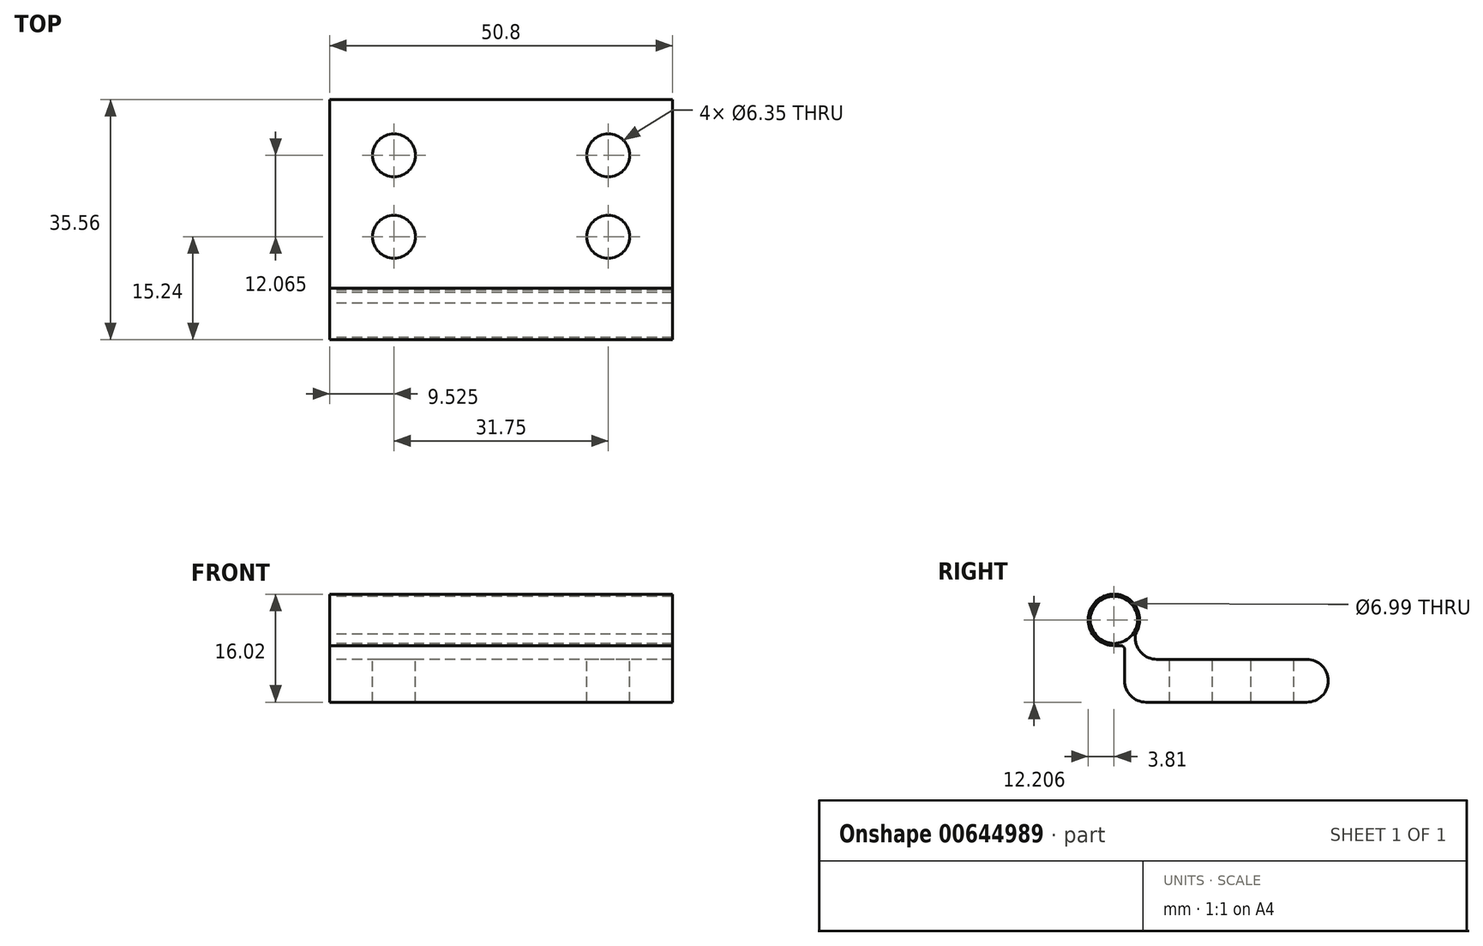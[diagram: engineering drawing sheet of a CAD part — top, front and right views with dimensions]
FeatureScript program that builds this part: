
annotation { "Feature Type Name" : "Feature", "Feature Type Description" : "" }
export const myFeature = defineFeature(function(context is Context, id is Id, definition is map)
    precondition{}
    {
        {
            var Q0;
            Q0=qCreatedBy(makeId("Right.planeOp"),FACE);
            var sketch = newSketch(context, id + "F0", { "sketchPlane" : qUnion([Q0])});
            skLineSegment(sketch, "E0.bottom", {"start": v(9.53, 3.18) * mm, "end": v(-12.7, 3.18) * mm});
            skLineSegment(sketch, "E0.top", {"start": v(9.53, -3.18) * mm, "end": v(-12.7, -3.18) * mm});
            skLineSegment(sketch, "E0.left", {"start": v(12.7, 0) * mm, "end": v(12.7, 0) * mm});
            skPoint(sketch, "E0.middle", {"position": v(0, 0) * mm});
            skLineSegment(sketch, "E1", {"start": v(-12.7, 3.18) * mm, "end": v(-12.7, 3.18) * mm});
            skArc(sketch, "E2", {"start": v(-15.88, 6.92) * mm, "mid": v(-20.85, 12.38) * mm, "end": v(-19.05, 5.22) * mm});
            skPoint(sketch, "E2.centerSnap0", {"position": v(-19.05, 3.18) * mm});
            skCircle(sketch, "E3", {"center": v(-19.05, 9.03) * mm, "radius": 3.5 * mm});
            skLineSegment(sketch, "E4", {"start": v(-14.29, -3.17) * mm, "end": v(-12.7, -3.17) * mm});
            skLineSegment(sketch, "E5", {"start": v(-15.88, 6.35) * mm, "end": v(-15.88, 6.92) * mm});
            skLineSegment(sketch, "E6", {"start": v(-19.05, 5.22) * mm, "end": v(-18.03, 5.22) * mm});
            skLineSegment(sketch, "E7", {"start": v(-17.46, 0) * mm, "end": v(-17.46, 4.65) * mm});
            skPoint(sketch, "E8.visualSharp", {"position": v(-17.46, -3.18) * mm});
            skArc(sketch, "E8.filletArc", {"start": v(-17.46, 0) * mm, "mid": v(-16.53, -2.25) * mm, "end": v(-14.29, -3.17) * mm});
            skPoint(sketch, "E9.visualSharp", {"position": v(12.7, -3.18) * mm});
            skArc(sketch, "E9.filletArc", {"start": v(9.53, -3.18) * mm, "mid": v(11.77, -2.25) * mm, "end": v(12.7, 0) * mm});
            skPoint(sketch, "E10.visualSharp", {"position": v(12.7, 3.18) * mm});
            skArc(sketch, "E10.filletArc", {"start": v(12.7, 0) * mm, "mid": v(11.77, 2.25) * mm, "end": v(9.53, 3.18) * mm});
            skPoint(sketch, "E11.visualSharp", {"position": v(-15.88, 3.18) * mm});
            skArc(sketch, "E11.filletArc", {"start": v(-15.88, 6.35) * mm, "mid": v(-14.95, 4.1) * mm, "end": v(-12.7, 3.18) * mm});
            skPoint(sketch, "E12.visualSharp", {"position": v(-17.46, 5.22) * mm});
            skArc(sketch, "E12.filletArc", {"start": v(-17.46, 4.65) * mm, "mid": v(-17.63, 5.05) * mm, "end": v(-18.03, 5.22) * mm});
            skLineSegment(sketch, "E13", {"start": v(-19.05, 9.03) * mm, "end": v(-19.05, -3.17) * mm});
            skSolve(sketch);
        }
        {
            var Q0;
            Q0=makeQuery(id+"F0.imprint","IMPRINT",FACE,{"disambiguationData":[TD([[makeQuery(id+"F0.imprint","IMPRINT",EDGE,{"derivedFrom":sQuery(id+"F0.wireOp",EDGE,"E0.bottom")}),1.0]])]});
            extrude(context, id + "F1", {"entities" : qUnion([Q0]), "depth" : 50.8 * mm, "offsetDistance" : 25.4 * mm});
        }
        {
            var Q0;
            Q0=makeQuery(id+"F1.opExtrude","SWEPT_FACE",FACE,{"disambiguationData":[OSD([sQuery(id+"F0.wireOp",EDGE,"E0.bottom")])]});
            var sketch = newSketch(context, id + "F2", { "sketchPlane" : qUnion([Q0])});
            skPoint(sketch, "E14", {"position": v(9.52, 4.44) * mm});
            skPoint(sketch, "E15", {"position": v(9.52, -7.62) * mm});
            skPoint(sketch, "E16", {"position": v(41.28, 4.45) * mm});
            skPoint(sketch, "E17", {"position": v(41.28, -7.62) * mm});
            skCircle(sketch, "E18", {"center": v(9.52, 4.44) * mm, "radius": 3.18 * mm});
            skCircle(sketch, "E19", {"center": v(9.52, -7.62) * mm, "radius": 3.18 * mm});
            skCircle(sketch, "E20", {"center": v(41.28, 4.45) * mm, "radius": 3.18 * mm});
            skCircle(sketch, "E21", {"center": v(41.28, -7.62) * mm, "radius": 3.18 * mm});
            skSolve(sketch);
        }
        {
            var Q0;
            Q0=makeQuery(id+"F2.imprint","IMPRINT",FACE,{"disambiguationData":[TD([[makeQuery(id+"F2.imprint","IMPRINT",EDGE,{"derivedFrom":sQuery(id+"F2.wireOp",EDGE,"E21")}),1.0]])]});
            var Q1;
            Q1=makeQuery(id+"F2.imprint","IMPRINT",FACE,{"disambiguationData":[TD([[makeQuery(id+"F2.imprint","IMPRINT",EDGE,{"derivedFrom":sQuery(id+"F2.wireOp",EDGE,"E20")}),1.0]])]});
            var Q2;
            Q2=makeQuery(id+"F2.imprint","IMPRINT",FACE,{"disambiguationData":[TD([[makeQuery(id+"F2.imprint","IMPRINT",EDGE,{"derivedFrom":sQuery(id+"F2.wireOp",EDGE,"E18")}),1.0]])]});
            var Q3;
            Q3=makeQuery(id+"F2.imprint","IMPRINT",FACE,{"disambiguationData":[TD([[makeQuery(id+"F2.imprint","IMPRINT",EDGE,{"derivedFrom":sQuery(id+"F2.wireOp",EDGE,"E19")}),1.0]])]});
            extrude(context, id + "F3", {"entities" : qUnion([Q0, Q1, Q2, Q3]), "operationType" : NewBodyOperationType.REMOVE, "oppositeDirection" : true, "depth" : 25.4 * mm, "offsetDistance" : 25.4 * mm});
        }
    });
